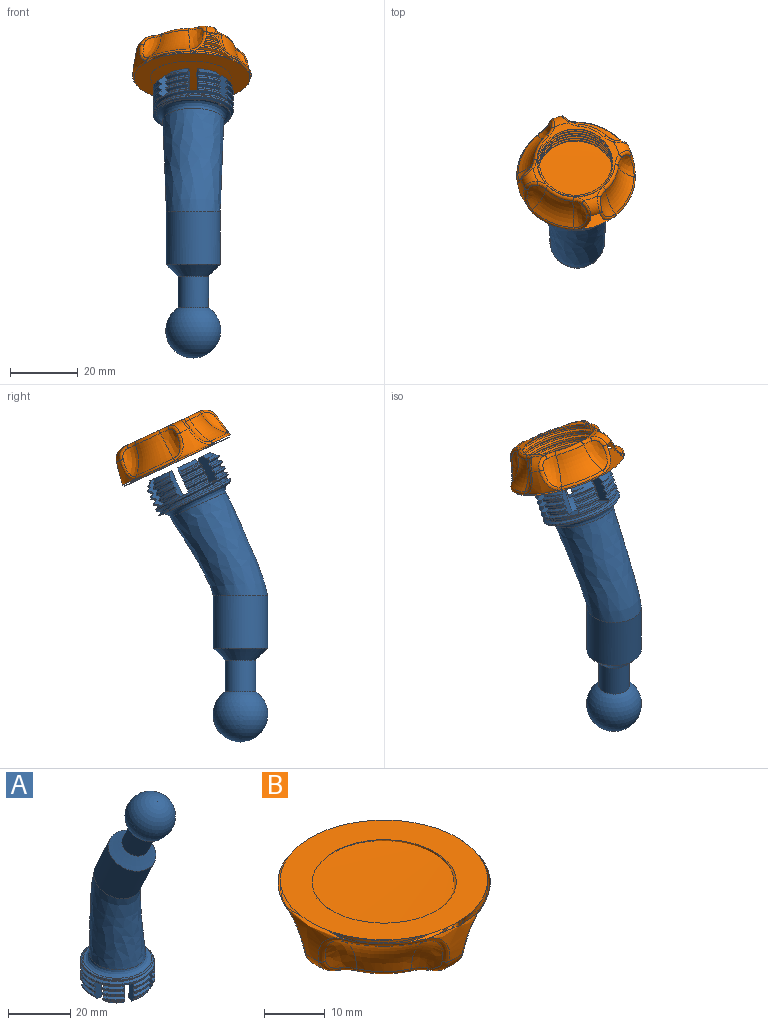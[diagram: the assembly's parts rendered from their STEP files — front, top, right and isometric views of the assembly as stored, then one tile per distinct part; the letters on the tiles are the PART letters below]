
ASSEMBLY  parts=2 mates=1
PART A: 153 faces, bbox 24.5x37.4x82.8 mm
  f0: plane 5.36x4.78mm, normal (0,0,-1), area 10.3mm2, adj f20,f27,f116,f145
  f1: plane 6x2.25mm, normal (0,0,-1), area 10.3mm2, adj f25,f28,f117,f144
  f2: plane 5.36x4.78mm, normal (0,0,-1), area 10.3mm2, adj f23,f26,f118,f146
  f3: plane 5.85x2.98mm, normal (0,0,-1), area 10.3mm2, adj f21,f24,f119,f147
  f4: plane 5.67x3.96mm, normal (0,0,-1), area 10.3mm2, adj f15,f22,f120,f148
  f5: cylinder r=11mm len=5.23mm, axis (0,0,1), area 3.4mm2, adj f10,f20,f27,f53,f145
  f6: cylinder r=11mm len=6.53mm, axis (0,0,1), area 2mm2, adj f8,f18,f19,f149
  f7: cylinder r=11mm len=3.14mm, axis (0,0,1), area 0.2mm2, adj f9,f17,f151
  f8: bspline ~20.55x6.37mm, area 5.6mm2, adj f6,f18,f19,f112,f150
  f9: bspline ~17.8x13.7mm, area 0.5mm2, adj f7,f17,f151
  f10: bspline ~10.28x6.37mm, area 0.4mm2, adj f5,f27,f145
  f11: bspline ~11.87x4.18mm, area 1.8mm2, adj f25,f28,f34,f144
  f12: bspline ~10.28x6.37mm, area 3.3mm2, adj f23,f26,f38,f146
  f13: bspline ~20.55x6.37mm, area 4.8mm2, adj f21,f24,f41,f147
  f14: bspline ~17.8x13.7mm, area 6.3mm2, adj f15,f22,f44,f148
  f15: plane 8.76x4.91mm, normal (-0.99,0.14,0), area 26.9mm2, adj f4,f14,f44,f45,f46,f66,f67,f68
  f16: plane 8.76x4.91mm, normal (0.99,0.14,0), area 26.9mm2, adj f30,f50,f51,f52,f71,f72,f73,f91
  f17: plane 8.13x3.18mm, normal (-0.73,-0.69,0), area 26.9mm2, adj f7,f9,f30,f50,f51,f52,f71,f72
  f18: plane 8.07x3.68mm, normal (0.51,0.86,0), area 26.9mm2, adj f6,f8,f29,f47,f48,f49,f59,f69
  f19: plane 8.01x4.19mm, normal (0.08,-1,0), area 26.8mm2, adj f6,f8,f29,f47,f48,f49,f59,f69
  f20: plane 8.05x3.96mm, normal (-0.36,0.93,0), area 26.7mm2, adj f0,f5,f31,f32,f33,f53,f54,f55
  f21: plane 8.07x3.68mm, normal (-0.51,0.86,0), area 26.9mm2, adj f3,f13,f41,f42,f43,f63,f64,f65
  f22: plane 8x3.04mm, normal (0.73,-0.69,0), area 26.9mm2, adj f4,f14,f44,f45,f46,f66,f67,f68
  f23: plane 8.05x3.96mm, normal (0.36,0.93,0), area 26.7mm2, adj f2,f12,f37,f38,f39,f40,f60,f61
  f24: plane 8.01x4.19mm, normal (-0.08,-1,0), area 26.8mm2, adj f3,f13,f37,f41,f42,f43,f63,f64
  f25: plane 8.39x4.39mm, normal (0.95,0.3,0), area 26.6mm2, adj f1,f11,f34,f35,f36,f37,f56,f57
  f26: plane 8.19x3.68mm, normal (-0.83,-0.56,0), area 26.7mm2, adj f2,f12,f37,f38,f39,f40,f60,f61
  f27: plane 8.19x3.68mm, normal (0.83,-0.56,0), area 26.6mm2, adj f0,f5,f10,f31,f32,f33,f53,f54
  f28: plane 8.39x4.39mm, normal (-0.95,0.3,0), area 26.6mm2, adj f1,f11,f34,f35,f36,f37,f56,f57
  f29: plane 5.85x2.98mm, normal (0,0,-1), area 10.3mm2, adj f18,f19,f121,f149
  f30: plane 5.67x3.96mm, normal (0,0,-1), area 10.3mm2, adj f16,f17,f122,f151
  f31: cylinder r=11mm len=5.23mm, axis (0,0,1), area 3.4mm2, adj f20,f27,f59,f76
  f32: cylinder r=11mm len=5.23mm, axis (0,0,1), area 3.4mm2, adj f20,f27,f55,f75
  f33: cylinder r=11mm len=5.23mm, axis (0,0,1), area 3.4mm2, adj f20,f27,f54,f74
  f34: cylinder r=11mm len=6.69mm, axis (0,0,1), area 3.4mm2, adj f11,f25,f28,f56
  f35: cylinder r=11mm len=6.69mm, axis (0,0,1), area 3.4mm2, adj f25,f28,f57,f77
  f36: cylinder r=11mm len=6.69mm, axis (0,0,1), area 3.4mm2, adj f25,f28,f58,f78
  f37: cylinder r=11mm len=22mm, axis (0,0,1), area 47.9mm2, adj f23,f24,f25,f26,f28,f59,f79,f82
  f38: cylinder r=11mm len=5.23mm, axis (0,0,1), area 3.4mm2, adj f12,f23,f26,f60
  f39: cylinder r=11mm len=5.23mm, axis (0,0,1), area 3.4mm2, adj f23,f26,f61,f80
  f40: cylinder r=11mm len=5.23mm, axis (0,0,1), area 3.4mm2, adj f23,f26,f62,f81
  f41: cylinder r=11mm len=6.53mm, axis (0,0,1), area 3.4mm2, adj f13,f21,f24,f65
  f42: cylinder r=11mm len=6.53mm, axis (0,0,1), area 3.4mm2, adj f21,f24,f64,f83
  f43: cylinder r=11mm len=6.53mm, axis (0,0,1), area 3.4mm2, adj f21,f24,f63,f84
  f44: cylinder r=11mm len=6.03mm, axis (0,0,1), area 3.4mm2, adj f14,f15,f22,f66
  f45: cylinder r=11mm len=6.03mm, axis (0,0,1), area 3.4mm2, adj f15,f22,f67,f86
  f46: cylinder r=11mm len=6.03mm, axis (0,0,1), area 3.4mm2, adj f15,f22,f68,f87
  f47: cylinder r=11mm len=6.53mm, axis (0,0,1), area 3.4mm2, adj f18,f19,f59,f90
  f48: cylinder r=11mm len=6.53mm, axis (0,0,1), area 3.4mm2, adj f18,f19,f70,f89
  f49: cylinder r=11mm len=6.53mm, axis (0,0,1), area 3.4mm2, adj f18,f19,f69,f88
  f50: cylinder r=11mm len=6.03mm, axis (0,0,1), area 3.4mm2, adj f16,f17,f73,f93
  f51: cylinder r=11mm len=6.03mm, axis (0,0,1), area 3.4mm2, adj f16,f17,f72,f92
  f52: cylinder r=11mm len=6.03mm, axis (0,0,1), area 3.4mm2, adj f16,f17,f71,f91
  f53: bspline ~10.28x6.37mm, area 7.1mm2, adj f5,f20,f27,f108
  f54: bspline ~10.28x6.37mm, area 7.1mm2, adj f20,f27,f33,f107
  f55: bspline ~10.28x6.37mm, area 7.1mm2, adj f20,f27,f32,f106
  f56: bspline ~11.87x4.18mm, area 7.1mm2, adj f25,f28,f34,f96
  f57: bspline ~11.87x4.18mm, area 7.1mm2, adj f25,f28,f35,f95
  f58: bspline ~11.87x4.18mm, area 7.1mm2, adj f25,f28,f36,f94
  f59: bspline ~27.4x23.73mm, area 101.2mm2, adj f18,f19,f20,f27,f28,f31,f37,f47
  f60: bspline ~10.28x6.37mm, area 7.1mm2, adj f23,f26,f38,f99
  f61: bspline ~10.28x6.37mm, area 7.1mm2, adj f23,f26,f39,f98
  f62: bspline ~10.28x6.37mm, area 7.1mm2, adj f23,f26,f40,f97
  f63: bspline ~20.55x6.37mm, area 7.1mm2, adj f21,f24,f43,f100
  f64: bspline ~20.55x6.37mm, area 7.1mm2, adj f21,f24,f42,f101
  f65: bspline ~20.55x6.37mm, area 7.1mm2, adj f21,f24,f41,f102
  f66: bspline ~17.8x13.7mm, area 7.1mm2, adj f15,f22,f44,f105
  f67: bspline ~17.8x13.7mm, area 7.1mm2, adj f15,f22,f45,f104
  f68: bspline ~17.8x13.7mm, area 7.1mm2, adj f15,f22,f46,f103
  f69: bspline ~20.55x6.37mm, area 7.1mm2, adj f18,f19,f49,f111
  f70: bspline ~20.55x6.37mm, area 7.1mm2, adj f18,f19,f48,f110
  f71: bspline ~17.8x13.7mm, area 7.1mm2, adj f16,f17,f52,f114
  f72: bspline ~17.8x13.7mm, area 7.1mm2, adj f16,f17,f51,f113
  f73: bspline ~17.8x13.7mm, area 7.1mm2, adj f16,f17,f50,f109
  f74: bspline ~10.28x6.37mm, area 7.1mm2, adj f20,f27,f33,f108
  f75: bspline ~10.28x6.37mm, area 7.1mm2, adj f20,f27,f32,f107
  f76: bspline ~10.28x6.37mm, area 7.1mm2, adj f20,f27,f31,f106
  f77: bspline ~11.87x4.18mm, area 7.1mm2, adj f25,f28,f35,f96
  f78: bspline ~11.87x4.18mm, area 7.1mm2, adj f25,f28,f36,f95
  f79: bspline ~11.87x4.18mm, area 7.1mm2, adj f25,f28,f37,f94
  f80: bspline ~10.28x6.37mm, area 7.1mm2, adj f23,f26,f39,f99
  f81: bspline ~10.28x6.37mm, area 7.1mm2, adj f23,f26,f40,f98
  f82: bspline ~10.28x6.37mm, area 7.1mm2, adj f23,f26,f37,f97
  f83: bspline ~20.55x6.37mm, area 7.1mm2, adj f21,f24,f42,f102
  f84: bspline ~20.55x6.37mm, area 7.1mm2, adj f21,f24,f43,f101
  f85: bspline ~27.4x23.73mm, area 98mm2, adj f15,f21,f22,f24,f37,f100,f103,f109
  f86: bspline ~17.8x13.7mm, area 7.1mm2, adj f15,f22,f45,f105
  f87: bspline ~17.8x13.7mm, area 7.1mm2, adj f15,f22,f46,f104
  f88: bspline ~20.55x6.37mm, area 7.1mm2, adj f18,f19,f49,f112
  f89: bspline ~20.55x6.37mm, area 7.1mm2, adj f18,f19,f48,f111
  f90: bspline ~20.55x6.37mm, area 7.1mm2, adj f18,f19,f47,f110
  f91: bspline ~17.8x13.7mm, area 7.1mm2, adj f16,f17,f52,f115
  f92: bspline ~17.8x13.7mm, area 7.1mm2, adj f16,f17,f51,f114
  f93: bspline ~17.8x13.7mm, area 7.1mm2, adj f16,f17,f50,f113
  f94: cylinder r=11.87mm len=7.22mm, axis (0,0,1), area 3.7mm2, adj f25,f28,f58,f79
  f95: cylinder r=11.87mm len=7.22mm, axis (0,0,1), area 3.7mm2, adj f25,f28,f57,f78
  f96: cylinder r=11.87mm len=7.22mm, axis (0,0,1), area 3.7mm2, adj f25,f28,f56,f77
  f97: cylinder r=11.87mm len=5.65mm, axis (0,0,1), area 3.7mm2, adj f23,f26,f62,f82
  f98: cylinder r=11.87mm len=5.65mm, axis (0,0,1), area 3.7mm2, adj f23,f26,f61,f81
  f99: cylinder r=11.87mm len=5.65mm, axis (0,0,1), area 3.7mm2, adj f23,f26,f60,f80
  f100: cylinder r=11.87mm len=7.04mm, axis (0,0,1), area 3.7mm2, adj f21,f24,f63,f85
  f101: cylinder r=11.87mm len=7.04mm, axis (0,0,1), area 3.7mm2, adj f21,f24,f64,f84
  f102: cylinder r=11.87mm len=7.04mm, axis (0,0,1), area 3.7mm2, adj f21,f24,f65,f83
  f103: cylinder r=11.87mm len=6.51mm, axis (0,0,1), area 3.7mm2, adj f15,f22,f68,f85
  f104: cylinder r=11.87mm len=6.51mm, axis (0,0,1), area 3.7mm2, adj f15,f22,f67,f87
  f105: cylinder r=11.87mm len=6.51mm, axis (0,0,1), area 3.7mm2, adj f15,f22,f66,f86
  f106: cylinder r=11.87mm len=5.65mm, axis (0,0,1), area 3.7mm2, adj f20,f27,f55,f76
  f107: cylinder r=11.87mm len=5.65mm, axis (0,0,1), area 3.7mm2, adj f20,f27,f54,f75
  f108: cylinder r=11.87mm len=5.65mm, axis (0,0,1), area 3.7mm2, adj f20,f27,f53,f74
  f109: cylinder r=11.87mm len=23.73mm, axis (0,0,1), area 49.8mm2, adj f16,f17,f18,f59,f73,f85,f136,f137
  f110: cylinder r=11.87mm len=7.04mm, axis (0,0,1), area 3.7mm2, adj f18,f19,f70,f90
  f111: cylinder r=11.87mm len=7.04mm, axis (0,0,1), area 3.7mm2, adj f18,f19,f69,f89
  f112: cylinder r=11.87mm len=7.04mm, axis (0,0,1), area 3.1mm2, adj f8,f18,f19,f88,f150
  f113: cylinder r=11.87mm len=6.51mm, axis (0,0,1), area 3.7mm2, adj f16,f17,f72,f93
  f114: cylinder r=11.87mm len=6.51mm, axis (0,0,1), area 3.7mm2, adj f16,f17,f71,f92
  f115: cylinder r=11.87mm len=6.51mm, axis (0,0,1), area 1.1mm2, adj f16,f17,f91,f151
  f116: torus R=9.37mm, axis (0,0,1), area 10.3mm2, adj f0,f20,f27,f124
  f117: torus R=9.37mm, axis (0,0,1), area 10.3mm2, adj f1,f25,f28,f125
  f118: torus R=9.37mm, axis (0,0,1), area 10.3mm2, adj f2,f23,f26,f126
  f119: torus R=9.37mm, axis (0,0,1), area 10.3mm2, adj f3,f21,f24,f127
  f120: torus R=9.37mm, axis (0,0,1), area 10.3mm2, adj f4,f15,f22,f128
  f121: torus R=9.37mm, axis (0,0,1), area 10.3mm2, adj f18,f19,f29,f129
  f122: torus R=9.37mm, axis (0,0,1), area 10.3mm2, adj f16,f17,f30,f130
  f123: sphere r=8mm, area 367.9mm2, adj f15,f16,f17,f18,f19,f20,f21,f22
  f124: cylinder r=8mm len=4mm, axis (0,0,-1), area 19.8mm2, adj f20,f27,f116,f123
  f125: cylinder r=8mm len=4.87mm, axis (0,0,-1), area 19.8mm2, adj f25,f28,f117,f123
  f126: cylinder r=8mm len=4mm, axis (0,0,-1), area 19.8mm2, adj f23,f26,f118,f123
  f127: cylinder r=8mm len=4.75mm, axis (0,0,-1), area 19.8mm2, adj f21,f24,f119,f123
  f128: cylinder r=8mm len=4.39mm, axis (0,0,-1), area 19.8mm2, adj f15,f22,f120,f123
  f129: cylinder r=8mm len=4.75mm, axis (0,0,-1), area 19.8mm2, adj f18,f19,f121,f123
  f130: cylinder r=8mm len=4.39mm, axis (0,0,-1), area 19.8mm2, adj f16,f17,f122,f123
  f131: cylinder r=4.5mm len=12.2mm, axis (0,-0.42,0.91), area 262mm2, adj f132,f134
  f132: sphere r=8.1mm, area 755mm2, adj f131
  f133: cylinder r=8mm len=21.05mm, axis (0,-0.42,0.91), area 779.1mm2, adj f134,f135
  f134: cone r=8mm half-angle=45deg, axis (0,0.42,-0.91), area 194.4mm2, adj f131,f133
  f135: bspline ~33.38x18.45mm, area 1551.7mm2, adj f133,f152
  f136: plane 22.89x22.88mm, normal (0,0,1), area 31.9mm2, adj f37,f59,f85,f109,f152
  f137: plane 4.76x3.86mm, normal (0,0,-1), area 11.2mm2, adj f15,f16,f85,f109,f123
  f138: plane 4.97x4.76mm, normal (0,0,-1), area 11.3mm2, adj f17,f18,f109,f123
  f139: plane 4.59x3.54mm, normal (0,0,-1), area 10.9mm2, adj f19,f20,f59,f123
  f140: plane 4.48x4.46mm, normal (0,0,-1), area 9.7mm2, adj f21,f22,f85,f123
  f141: plane 3.76x3.3mm, normal (0,0,-1), area 8.5mm2, adj f23,f24,f37,f123
  f142: plane 4.3x4.02mm, normal (0,0,-1), area 8.5mm2, adj f25,f26,f37,f123
  f143: plane 4.47x4.2mm, normal (0,0,-1), area 9.3mm2, adj f27,f28,f59,f123
  f144: cone r=9.87mm half-angle=45deg, axis (0,0,1), area 12.6mm2, adj f1,f11,f25,f28
  f145: cone r=9.87mm half-angle=45deg, axis (0,0,1), area 10.8mm2, adj f0,f5,f10,f20,f27
  f146: cone r=9.87mm half-angle=45deg, axis (0,0,1), area 14.4mm2, adj f2,f12,f23,f26
  f147: cone r=9.87mm half-angle=45deg, axis (0,0,1), area 16.2mm2, adj f3,f13,f21,f24
  f148: cone r=9.87mm half-angle=45deg, axis (0,0,1), area 18.1mm2, adj f4,f14,f15,f22
  f149: cone r=9.87mm half-angle=45deg, axis (0,0,1), area 10.3mm2, adj f6,f18,f19,f29
  f150: cone r=9.87mm half-angle=45deg, axis (0,0,1), area 1.8mm2, adj f8,f18,f112
  f151: cone r=9.87mm half-angle=45deg, axis (0,0,1), area 18.3mm2, adj f7,f9,f16,f17,f30,f115
  f152: bspline ~21.99x21.99mm, area 187.2mm2, adj f37,f85,f135,f136
PART B: 57 faces, bbox 48.9x48.9x12.6 mm
  f0: torus R=24.16mm, axis (0,0,1), area 107.6mm2, adj f12,f15,f27,f28
  f1: torus R=24.16mm, axis (0,0,1), area 107.6mm2, adj f14,f17,f51,f52
  f2: torus R=24.16mm, axis (0,0,1), area 107.6mm2, adj f16,f18,f43,f44
  f3: bspline ~24.81x24.8mm, area 380.9mm2, adj f4,f5,f6,f7,f10
  f4: bspline ~24.81x24.66mm, area 196.9mm2, adj f3,f5,f6,f8,f10
  f5: plane 26.05x26.05mm, normal (0,0,-1), area 68.8mm2, adj f3,f4,f7,f8,f20,f21,f22,f23
  f6: plane 34.5x34.5mm, normal (0,0,1), area 474mm2, adj f3,f4,f7,f8,f10,f56
  f7: cone r=10.5mm half-angle=4.8deg, axis (0,0,1), area 213.9mm2, adj f3,f5,f6,f8
  f8: bspline ~24.7x24.66mm, area 327.7mm2, adj f4,f5,f6,f7
  f9: torus R=24.16mm, axis (0,0,1), area 107.6mm2, adj f13,f19,f35,f36
  f10: cylinder r=12.32mm len=1.49mm, axis (0,0,1), area 0mm2, adj f3,f4,f6
  f11: revolved ~34.99x34.99mm, area 164.4mm2, adj f20,f21,f22,f23,f26,f28,f30,f34
  f12: bspline ~9.77x8.4mm, area 36.3mm2, adj f0,f29,f30,f31
  f13: bspline ~10.69x9.09mm, area 36.3mm2, adj f9,f32,f33,f34
  f14: bspline ~9.77x8.4mm, area 36.3mm2, adj f1,f53,f54,f55
  f15: bspline ~10.69x9.09mm, area 36.3mm2, adj f0,f24,f25,f26
  f16: bspline ~9.77x8.4mm, area 36.3mm2, adj f2,f45,f46,f47
  f17: bspline ~10.69x9.09mm, area 36.3mm2, adj f1,f48,f49,f50
  f18: bspline ~10.69x9.09mm, area 36.3mm2, adj f2,f40,f41,f42
  f19: bspline ~9.77x8.4mm, area 36.3mm2, adj f9,f37,f38,f39
  f20: torus R=12.86mm, axis (0,0,1), area 16.8mm2, adj f5,f11,f47,f48
  f21: torus R=12.86mm, axis (0,0,1), area 16.8mm2, adj f5,f11,f39,f40
  f22: torus R=12.86mm, axis (0,0,1), area 16.8mm2, adj f5,f11,f31,f32
  f23: torus R=12.86mm, axis (0,0,1), area 16.8mm2, adj f5,f11,f24,f55
  f24: bspline ~5.13x4.15mm, area 6.7mm2, adj f15,f23,f25,f26
  f25: bspline ~4.63x4.11mm, area 4.5mm2, adj f5,f15,f24,f27
  f26: bspline ~7.87x6.17mm, area 9.5mm2, adj f11,f15,f24,f28
  f27: torus R=11.54mm, axis (0,0,-1), area 13.2mm2, adj f0,f5,f25,f29
  f28: torus R=16.5mm, axis (0,0,-1), area 12.7mm2, adj f0,f11,f26,f30
  f29: bspline ~4.63x4.11mm, area 4.5mm2, adj f5,f12,f27,f31
  f30: bspline ~7.87x6.17mm, area 9.5mm2, adj f11,f12,f28,f31
  f31: bspline ~5.13x4.15mm, area 6.7mm2, adj f12,f22,f29,f30
  f32: bspline ~5.13x4.15mm, area 6.7mm2, adj f13,f22,f33,f34
  f33: bspline ~4.63x4.11mm, area 4.5mm2, adj f5,f13,f32,f35
  f34: bspline ~7.87x6.17mm, area 9.5mm2, adj f11,f13,f32,f36
  f35: torus R=11.54mm, axis (0,0,-1), area 13.2mm2, adj f5,f9,f33,f37
  f36: torus R=16.5mm, axis (0,0,-1), area 12.7mm2, adj f9,f11,f34,f38
  f37: bspline ~4.63x4.11mm, area 4.5mm2, adj f5,f19,f35,f39
  f38: bspline ~7.87x6.17mm, area 9.5mm2, adj f11,f19,f36,f39
  f39: bspline ~5.13x4.15mm, area 6.7mm2, adj f19,f21,f37,f38
  f40: bspline ~5.13x4.15mm, area 6.7mm2, adj f18,f21,f41,f42
  f41: bspline ~4.63x4.11mm, area 4.5mm2, adj f5,f18,f40,f43
  f42: bspline ~7.87x6.17mm, area 9.5mm2, adj f11,f18,f40,f44
  f43: torus R=11.54mm, axis (0,0,-1), area 13.2mm2, adj f2,f5,f41,f45
  f44: torus R=16.5mm, axis (0,0,-1), area 12.7mm2, adj f2,f11,f42,f46
  f45: bspline ~4.63x4.11mm, area 4.5mm2, adj f5,f16,f43,f47
  f46: bspline ~7.87x6.17mm, area 9.5mm2, adj f11,f16,f44,f47
  f47: bspline ~5.13x4.15mm, area 6.7mm2, adj f16,f20,f45,f46
  f48: bspline ~5.13x4.15mm, area 6.7mm2, adj f17,f20,f49,f50
  f49: bspline ~4.63x4.11mm, area 4.5mm2, adj f5,f17,f48,f51
  f50: bspline ~7.87x6.17mm, area 9.5mm2, adj f11,f17,f48,f52
  f51: torus R=11.54mm, axis (0,0,-1), area 13.2mm2, adj f1,f5,f49,f53
  f52: torus R=16.5mm, axis (0,0,-1), area 12.7mm2, adj f1,f11,f50,f54
  f53: bspline ~4.63x4.11mm, area 4.5mm2, adj f5,f14,f51,f55
  f54: bspline ~7.87x6.17mm, area 9.5mm2, adj f11,f14,f52,f55
  f55: bspline ~5.13x4.15mm, area 6.7mm2, adj f14,f23,f53,f54
  f56: cone r=17.1mm half-angle=44.7deg, axis (0,0,-1), area 61.8mm2, adj f6,f11
PLACE A rot(axis=(1,0,0),155deg) t=(0,17.75,45.81)mm
PLACE B rot(axis=(0.98,0.17,-0.04),155.4deg) t=(-0.38,23.75,58.17)mm
MATE cylindrical A.f94 <-> B.f6  axis (0,0.42,0.91) through (0,15.21,40.38)mm
